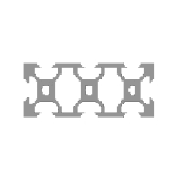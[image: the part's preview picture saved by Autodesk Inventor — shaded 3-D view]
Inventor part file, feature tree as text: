
AUTODESK INVENTOR PART (.ipt)
format: ipt  version: 2013 (Build 170138000, 138)  size: 248,832 bytes
history: native  units: mm
features: other x4, plane x3, split x2, sketch x2
ambient origin geometry x8: Origin, YZ Plane, XZ Plane, XY Plane, X Axis, Y Axis, Z Axis, Center Point
bodies: Solid1 (feature_tree), Body (feature_tree)
feature tree (11):
  other  "Driven Length"
  other  "Frame Generator"
  other  "Start Plane"
  other  "End Plane"
  plane  "Work Plane5"
  split  "Split1"
  plane  "Work Plane6"
  split  "Split2"
  sketch  "Sketch4"  dims[d0=10.0mm]
  plane  "Work Plane4"
  sketch  "Sketch5"  dims[d1=10.0mm d2=10.0mm d3=4.2mm d4=1.5mm d5=45.0deg d6=1.64mm d7=1.8mm d8=10.0mm d9=2.84mm d11=135.0deg d12=1.96mm d13=5.68mm d14=1.8mm d17=10.0mm d18=465.0mm d19=0.13mm d20=0.0mm d23=90.0deg d22=455.0mm]
